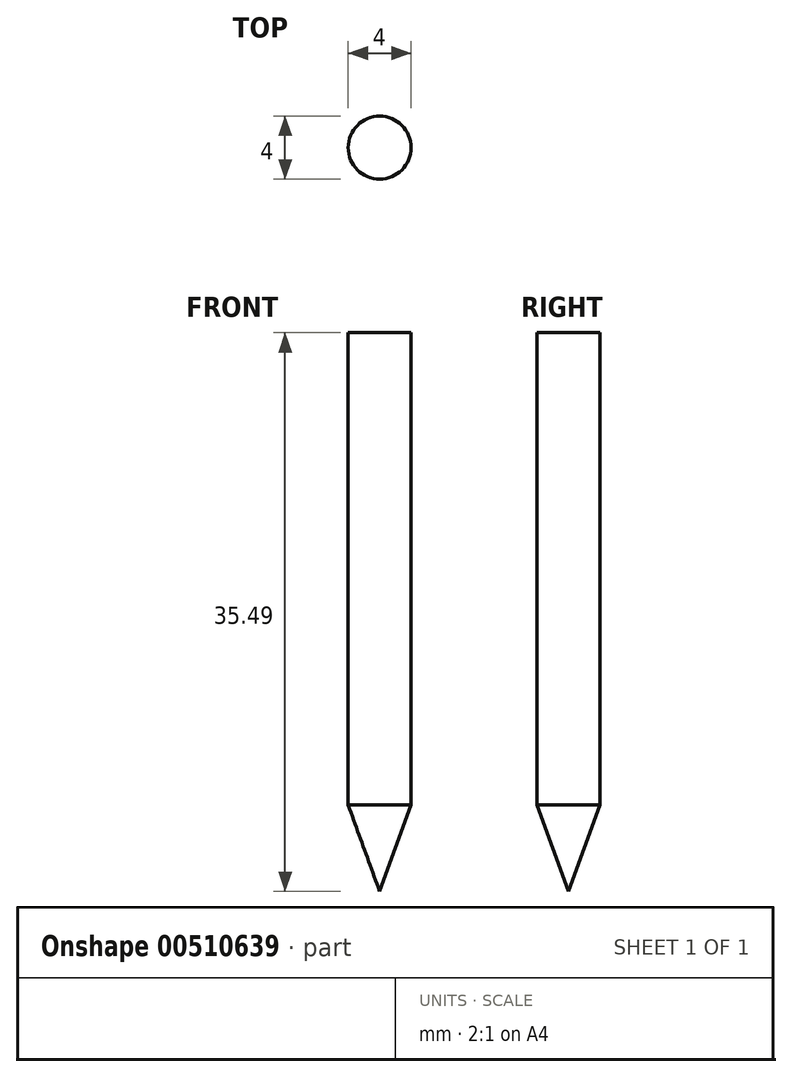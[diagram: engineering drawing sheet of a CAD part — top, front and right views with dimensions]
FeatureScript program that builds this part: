
annotation { "Feature Type Name" : "Feature", "Feature Type Description" : "" }
export const myFeature = defineFeature(function(context is Context, id is Id, definition is map)
    precondition{}
    {
        {
            var Q0;
            Q0=qCreatedBy(makeId("Top.planeOp"),FACE);
            var sketch = newSketch(context, id + "F0", { "sketchPlane" : qUnion([Q0])});
            skCircle(sketch, "E0", {"center": v(0, 0) * mm, "radius": 2 * mm});
            skSolve(sketch);
        }
        {
            var Q0;
            Q0 = qSketchRegion(id + "F0", true);
            extrude(context, id + "F1", {"entities" : qUnion([Q0]), "depth" : 30 * mm});
        }
        {
            var Q0;
            Q0 = qSketchRegion(id + "F0", true);
            extrude(context, id + "F2", {"entities" : qUnion([Q0]), "operationType" : NewBodyOperationType.ADD, "oppositeDirection" : true, "depth" : 6 * mm, "hasDraft" : true, "draftAngle" : 20 * degree, "draftPullDirection" : true});
        }
    });
